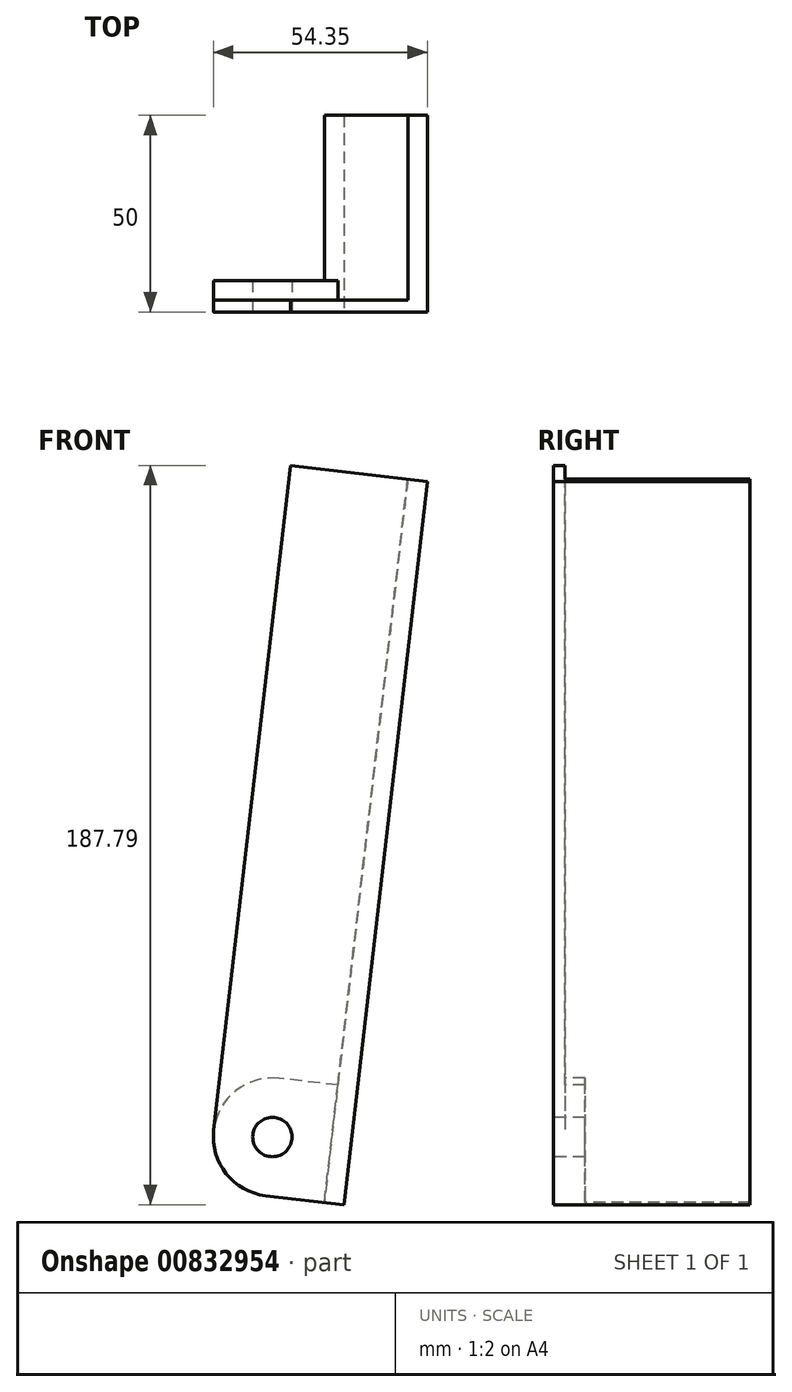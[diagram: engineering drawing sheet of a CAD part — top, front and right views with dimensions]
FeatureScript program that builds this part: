
annotation { "Feature Type Name" : "Feature", "Feature Type Description" : "" }
export const myFeature = defineFeature(function(context is Context, id is Id, definition is map)
    precondition{}
    {
        {
            var Q0;
            Q0=qCreatedBy(makeId("Front.planeOp"),FACE);
            var sketch = newSketch(context, id + "F0", { "sketchPlane" : qUnion([Q0])});
            skLineSegment(sketch, "E0", {"start": v(81.21, 183.78) * mm, "end": v(60, 0) * mm});
            skLineSegment(sketch, "E1.0", {"start": v(86.18, 183.2) * mm, "end": v(64.98, -0.57) * mm});
            skLineSegment(sketch, "E2", {"start": v(81.21, 183.78) * mm, "end": v(86.18, 183.2) * mm});
            skLineSegment(sketch, "E3", {"start": v(60, 0) * mm, "end": v(64.98, -0.57) * mm});
            skSolve(sketch);
        }
        {
            var Q0;
            Q0=makeQuery(id+"F0.imprint","IMPRINT",FACE,{"disambiguationData":[TD([[makeQuery(id+"F0.imprint","IMPRINT",EDGE,{"derivedFrom":sQuery(id+"F0.wireOp",EDGE,"E0")}),1.0]])]});
            extrude(context, id + "F1", {"entities" : qUnion([Q0]), "oppositeDirection" : true, "depth" : 50 * mm, "offsetDistance" : 25 * mm});
        }
        {
            var Q0;
            Q0=makeQuery(id+"F1.opExtrude","CAP_FACE",FACE,{"disambiguationData":[OSD([sQuery(id+"F0.wireOp",EDGE,"E0"),sQuery(id+"F0.wireOp",EDGE,"E1.0"),sQuery(id+"F0.wireOp",EDGE,"E2"),sQuery(id+"F0.wireOp",EDGE,"E3")])],"isStart":true});
            cPlane(context, id + "F2", {"entities" : qUnion([Q0]), "cplaneType" : CPlaneType.OFFSET, "offset" : 3 * mm, "oppositeDirection" : true, "width" : 150 * mm, "height" : 150 * mm});
        }
        {
            var Q0;
            Q0=qCreatedBy(id+"F2.planeOp",FACE);
            var sketch = newSketch(context, id + "F3", { "sketchPlane" : qUnion([Q0])});
            skLineSegment(sketch, "E4", {"start": v(60, 0) * mm, "end": v(63.45, 29.8) * mm});
            skLineSegment(sketch, "E5", {"start": v(63.45, 29.8) * mm, "end": v(48.55, 31.52) * mm});
            skLineSegment(sketch, "E6", {"start": v(45.1, 1.72) * mm, "end": v(60, 0) * mm});
            skArc(sketch, "E7", {"start": v(48.55, 31.52) * mm, "mid": v(31.93, 18.34) * mm, "end": v(45.1, 1.72) * mm});
            skCircle(sketch, "E8", {"center": v(46.83, 16.62) * mm, "radius": 5 * mm});
            skLineSegment(sketch, "E9", {"start": v(60, 0) * mm, "end": v(81.21, 183.78) * mm});
            skLineSegment(sketch, "E10", {"start": v(81.21, 183.78) * mm, "end": v(51.41, 187.22) * mm});
            skLineSegment(sketch, "E11", {"start": v(51.41, 187.22) * mm, "end": v(30.2, 3.44) * mm});
            skLineSegment(sketch, "E12", {"start": v(30.2, 3.44) * mm, "end": v(60, 0) * mm});
            skSolve(sketch);
        }
        {
            var Q0;
            Q0=makeQuery(id+"F3.imprint","IMPRINT",FACE,{"disambiguationData":[TD([[makeQuery(id+"F3.imprint","IMPRINT",EDGE,{"derivedFrom":sQuery(id+"F3.wireOp",EDGE,"E4")}),1.0]])]});
            var Q1;
            Q1=makeQuery(id+"F3.imprint","IMPRINT",FACE,{"disambiguationData":[TD([[makeQuery(id+"F3.imprint","IMPRINT",EDGE,{"derivedFrom":sQuery(id+"F3.wireOp",EDGE,"E4")}),1.0]])]});
            extrude(context, id + "F4", {"entities" : qUnion([Q0, Q1]), "operationType" : NewBodyOperationType.ADD, "oppositeDirection" : true, "depth" : 5 * mm, "offsetDistance" : 25 * mm});
        }
        {
            var Q0;
            Q0=makeQuery(id+"F3.imprint","IMPRINT",FACE,{"disambiguationData":[TD([[makeQuery(id+"F3.imprint","IMPRINT",EDGE,{"derivedFrom":sQuery(id+"F3.wireOp",EDGE,"E4")}),1.0]])]});
            var Q1;
            {var subQ2=sQuery(id+"F3.wireOp",EDGE,"E5");Q1=makeQuery(id+"F3.imprint","IMPRINT",FACE,{"disambiguationData":[TD([[makeQuery(id+"F3.imprint","IMPRINT",EDGE,{"derivedFrom":subQ2}),-1.0]])]});}
            extrude(context, id + "F5", {"entities" : qUnion([Q0, Q1]), "operationType" : NewBodyOperationType.ADD, "depth" : 3 * mm, "offsetDistance" : 25 * mm});
        }
    });
